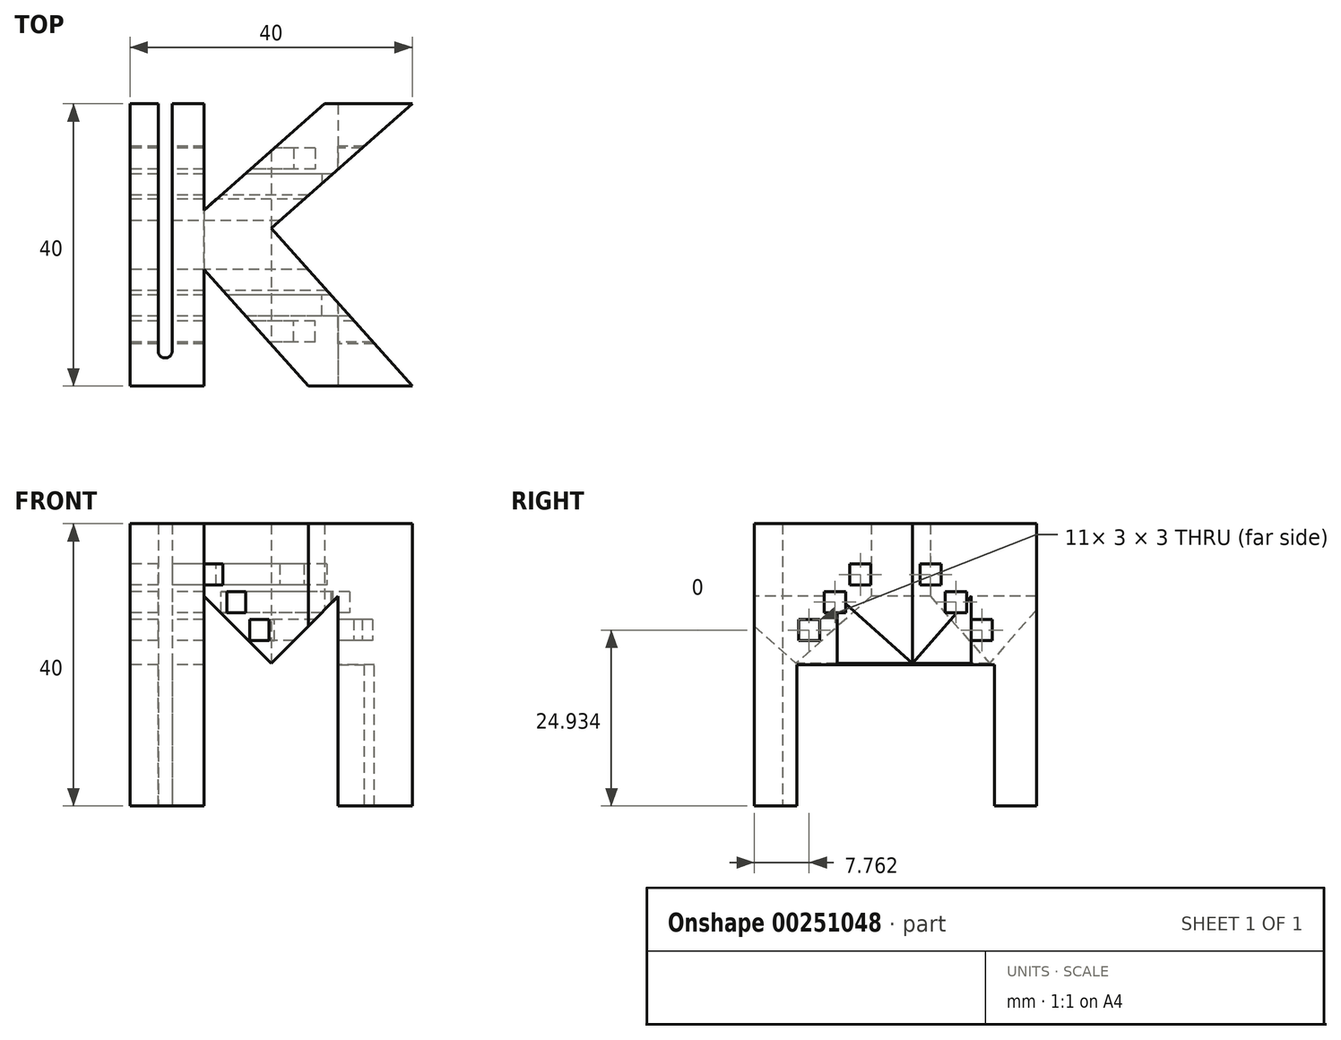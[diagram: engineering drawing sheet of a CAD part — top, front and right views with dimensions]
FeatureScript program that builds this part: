
annotation { "Feature Type Name" : "Feature", "Feature Type Description" : "" }
export const myFeature = defineFeature(function(context is Context, id is Id, definition is map)
    precondition{}
    {
        {
            var Q0;
            Q0=qCreatedBy(makeId("Top.planeOp"),FACE);
            var sketch = newSketch(context, id + "F0", { "sketchPlane" : qUnion([Q0])});
            skLineSegment(sketch, "E0.bottom", {"start": v(20, 20) * mm, "end": v(-20, 20) * mm});
            skLineSegment(sketch, "E0.top", {"start": v(20, -20) * mm, "end": v(-20, -20) * mm});
            skLineSegment(sketch, "E0.left", {"start": v(20, 20) * mm, "end": v(20, -20) * mm});
            skLineSegment(sketch, "E0.right", {"start": v(-20, 20) * mm, "end": v(-20, -20) * mm});
            skPoint(sketch, "E0.middle", {"position": v(0, 0) * mm});
            skLineSegment(sketch, "E1", {"start": v(-16, -15) * mm, "end": v(-16, 20) * mm});
            skLineSegment(sketch, "E2", {"start": v(-14, 20) * mm, "end": v(-14, -15) * mm});
            skLineSegment(sketch, "E3", {"start": v(-9.5, 20) * mm, "end": v(-9.5, -20) * mm});
            skLineSegment(sketch, "E4", {"start": v(-9.5, 4.95) * mm, "end": v(7.58, 20) * mm});
            skLineSegment(sketch, "E5", {"start": v(20, 20) * mm, "end": v(0, 2.39) * mm});
            skLineSegment(sketch, "E6", {"start": v(0, 2.39) * mm, "end": v(20, -20) * mm});
            skLineSegment(sketch, "E7", {"start": v(-9.5, -3.45) * mm, "end": v(5.28, -20) * mm});
            skArc(sketch, "E8", {"start": v(-16, -15) * mm, "mid": v(-15, -16) * mm, "end": v(-14, -15) * mm});
            skSolve(sketch);
        }
        {
            var Q0;
            {var subQ0=sQuery(id+"F0.wireOp",EDGE,"E4");Q0=makeQuery(id+"F0.imprint","IMPRINT",FACE,{"disambiguationData":[TD([[makeQuery(id+"F0.imprint","IMPRINT",EDGE,{"derivedFrom":subQ0}),-1.0]])]});}
            var Q1;
            {var subQ4=sQuery(id+"F0.wireOp",EDGE,"E2");Q1=makeQuery(id+"F0.imprint","IMPRINT",FACE,{"disambiguationData":[TD([[makeQuery(id+"F0.imprint","IMPRINT",EDGE,{"derivedFrom":subQ4}),1.0]])]});}
            var Q2;
            {var subQ0=sQuery(id+"F0.wireOp",EDGE,"E0.right");Q2=makeQuery(id+"F0.imprint","IMPRINT",FACE,{"disambiguationData":[TD([[makeQuery(id+"F0.imprint","IMPRINT",EDGE,{"derivedFrom":subQ0}),1.0]])]});}
            extrude(context, id + "F1", {"entities" : qUnion([Q0, Q1, Q2]), "depth" : 40 * mm});
        }
        {
            var Q0;
            Q0=makeQuery(id+"F1.opExtrude","SWEPT_FACE",FACE,{"disambiguationData":[OSD([sQuery(id+"F0.wireOp",EDGE,"E0.right")])]});
            var sketch = newSketch(context, id + "F2", { "sketchPlane" : qUnion([Q0])});
            skLineSegment(sketch, "E9", {"start": v(-14, 0) * mm, "end": v(-14, 20) * mm});
            skLineSegment(sketch, "E10", {"start": v(-14, 20) * mm, "end": v(14, 20) * mm});
            skLineSegment(sketch, "E11", {"start": v(14, 20) * mm, "end": v(14, 0) * mm});
            skLineSegment(sketch, "E12.bottom", {"start": v(-10.74, 23.43) * mm, "end": v(-13.74, 23.43) * mm});
            skLineSegment(sketch, "E12.top", {"start": v(-10.74, 26.43) * mm, "end": v(-13.74, 26.43) * mm});
            skLineSegment(sketch, "E12.left", {"start": v(-10.74, 23.43) * mm, "end": v(-10.74, 26.43) * mm});
            skLineSegment(sketch, "E12.right", {"start": v(-13.74, 23.43) * mm, "end": v(-13.74, 26.43) * mm});
            skPoint(sketch, "E12.middle", {"position": v(-12.24, 24.93) * mm});
            skLineSegment(sketch, "E13.bottom", {"start": v(-7.08, 27.4) * mm, "end": v(-10.08, 27.4) * mm});
            skLineSegment(sketch, "E13.top", {"start": v(-7.08, 30.4) * mm, "end": v(-10.08, 30.4) * mm});
            skLineSegment(sketch, "E13.left", {"start": v(-7.08, 27.4) * mm, "end": v(-7.08, 30.4) * mm});
            skLineSegment(sketch, "E13.right", {"start": v(-10.08, 27.4) * mm, "end": v(-10.08, 30.4) * mm});
            skPoint(sketch, "E13.middle", {"position": v(-8.58, 28.9) * mm});
            skLineSegment(sketch, "E14.bottom", {"start": v(-3.47, 31.3) * mm, "end": v(-6.47, 31.3) * mm});
            skLineSegment(sketch, "E14.top", {"start": v(-3.47, 34.3) * mm, "end": v(-6.47, 34.3) * mm});
            skLineSegment(sketch, "E14.left", {"start": v(-3.47, 31.3) * mm, "end": v(-3.47, 34.3) * mm});
            skLineSegment(sketch, "E14.right", {"start": v(-6.47, 31.3) * mm, "end": v(-6.47, 34.3) * mm});
            skPoint(sketch, "E14.middle", {"position": v(-4.97, 32.8) * mm});
            skLineSegment(sketch, "E15.MirrorCS", {"start": v(3.47, 31.3) * mm, "end": v(3.47, 34.3) * mm});
            skLineSegment(sketch, "E16.MirrorCS", {"start": v(3.47, 34.3) * mm, "end": v(6.47, 34.3) * mm});
            skLineSegment(sketch, "E17.MirrorCS", {"start": v(6.47, 31.3) * mm, "end": v(6.47, 34.3) * mm});
            skLineSegment(sketch, "E18.MirrorCS", {"start": v(3.47, 31.3) * mm, "end": v(6.47, 31.3) * mm});
            skLineSegment(sketch, "E19.MirrorCS", {"start": v(7.08, 30.4) * mm, "end": v(10.08, 30.4) * mm});
            skLineSegment(sketch, "E20.MirrorCS", {"start": v(10.08, 27.4) * mm, "end": v(10.08, 30.4) * mm});
            skLineSegment(sketch, "E21.MirrorCS", {"start": v(7.08, 27.4) * mm, "end": v(10.08, 27.4) * mm});
            skLineSegment(sketch, "E22.MirrorCS", {"start": v(7.08, 27.4) * mm, "end": v(7.08, 30.4) * mm});
            skLineSegment(sketch, "E23.MirrorCS", {"start": v(13.74, 23.43) * mm, "end": v(13.74, 26.43) * mm});
            skPoint(sketch, "E24.MirrorP", {"position": v(12.24, 24.93) * mm});
            skLineSegment(sketch, "E25.MirrorCS", {"start": v(10.74, 23.43) * mm, "end": v(13.74, 23.43) * mm});
            skLineSegment(sketch, "E26.MirrorCS", {"start": v(10.74, 23.43) * mm, "end": v(10.74, 26.43) * mm});
            skLineSegment(sketch, "E27.MirrorCS", {"start": v(10.74, 26.43) * mm, "end": v(13.74, 26.43) * mm});
            skPoint(sketch, "E28.MirrorP", {"position": v(8.58, 28.9) * mm});
            skPoint(sketch, "E29.MirrorP", {"position": v(4.97, 32.8) * mm});
            skSolve(sketch);
        }
        {
            var Q0;
            {var subQ0=sQuery(id+"F2.wireOp",EDGE,"E9");Q0=makeQuery(id+"F2.imprint","IMPRINT",FACE,{"disambiguationData":[TD([[makeQuery(id+"F2.imprint","IMPRINT",EDGE,{"derivedFrom":subQ0}),-1.0]])]});}
            extrude(context, id + "F3", {"entities" : qUnion([Q0]), "operationType" : NewBodyOperationType.REMOVE, "oppositeDirection" : true, "depth" : 40 * mm});
        }
        {
            var Q0;
            {var subQ0=sQuery(id+"F0.wireOp",EDGE,"E0.top");Q0=makeQuery(id+"F1.opExtrude","SWEPT_FACE",FACE,{"disambiguationData":[OSD([subQ0]),TDD([makeQuery(id+"F0.imprint","IMPRINT",EDGE,{"disambiguationData":[TD([[makeQuery(id+"F0.imprint","INTERSECT",VERTEX,{"derivedFrom":[subQ0,sQuery(id+"F0.wireOp",EDGE,"E0.right")]}),1.0]])],"derivedFrom":subQ0})])]});}
            var sketch = newSketch(context, id + "F4", { "sketchPlane" : qUnion([Q0])});
            skLineSegment(sketch, "E30", {"start": v(0, 20.21) * mm, "end": v(-9.5, 29.72) * mm});
            skLineSegment(sketch, "E31", {"start": v(0, 20.21) * mm, "end": v(9.5, 29.72) * mm});
            skLineSegment(sketch, "E32", {"start": v(9.5, 29.72) * mm, "end": v(9.5, 0) * mm});
            skLineSegment(sketch, "E33", {"start": v(-9.5, 29.72) * mm, "end": v(-9.5, 0) * mm});
            skLineSegment(sketch, "E34", {"start": v(-9.5, 0) * mm, "end": v(-20, 0) * mm});
            skLineSegment(sketch, "E35", {"start": v(-20, 0) * mm, "end": v(-20, 40) * mm});
            skLineSegment(sketch, "E36", {"start": v(-20, 40) * mm, "end": v(20, 40) * mm});
            skLineSegment(sketch, "E37", {"start": v(20, 40) * mm, "end": v(20, 0) * mm});
            skLineSegment(sketch, "E38", {"start": v(20, 0) * mm, "end": v(9.5, 0) * mm});
            skLineSegment(sketch, "E39", {"start": v(-9.5, 0) * mm, "end": v(9.5, 0) * mm});
            skSolve(sketch);
        }
        {
            var Q0;
            Q0=makeQuery(id+"F4.imprint","IMPRINT",FACE,{"disambiguationData":[TD([[makeQuery(id+"F4.imprint","IMPRINT",EDGE,{"derivedFrom":sQuery(id+"F4.wireOp",EDGE,"E30")}),1.0]])]});
            extrude(context, id + "F5", {"entities" : qUnion([Q0]), "operationType" : NewBodyOperationType.REMOVE, "oppositeDirection" : true, "depth" : 40 * mm});
        }
        {
            var Q0;
            Q0=makeQuery(id+"F2.imprint","IMPRINT",FACE,{"disambiguationData":[TD([[makeQuery(id+"F2.imprint","IMPRINT",EDGE,{"derivedFrom":sQuery(id+"F2.wireOp",EDGE,"E14.bottom")}),-1.0]])]});
            var Q1;
            Q1=makeQuery(id+"F2.imprint","IMPRINT",FACE,{"disambiguationData":[TD([[makeQuery(id+"F2.imprint","IMPRINT",EDGE,{"derivedFrom":sQuery(id+"F2.wireOp",EDGE,"E15.MirrorCS")}),-1.0]])]});
            var Q2;
            Q2=makeQuery(id+"F2.imprint","IMPRINT",FACE,{"disambiguationData":[TD([[makeQuery(id+"F2.imprint","IMPRINT",EDGE,{"derivedFrom":sQuery(id+"F2.wireOp",EDGE,"E13.bottom")}),-1.0]])]});
            var Q3;
            Q3=makeQuery(id+"F2.imprint","IMPRINT",FACE,{"disambiguationData":[TD([[makeQuery(id+"F2.imprint","IMPRINT",EDGE,{"derivedFrom":sQuery(id+"F2.wireOp",EDGE,"E12.bottom")}),-1.0]])]});
            var Q4;
            Q4=makeQuery(id+"F2.imprint","IMPRINT",FACE,{"disambiguationData":[TD([[makeQuery(id+"F2.imprint","IMPRINT",EDGE,{"derivedFrom":sQuery(id+"F2.wireOp",EDGE,"E19.MirrorCS")}),-1.0]])]});
            var Q5;
            Q5=makeQuery(id+"F2.imprint","IMPRINT",FACE,{"disambiguationData":[TD([[makeQuery(id+"F2.imprint","IMPRINT",EDGE,{"derivedFrom":sQuery(id+"F2.wireOp",EDGE,"E23.MirrorCS")}),1.0]])]});
            extrude(context, id + "F6", {"entities" : qUnion([Q0, Q1, Q2, Q3, Q4, Q5]), "operationType" : NewBodyOperationType.REMOVE, "oppositeDirection" : true, "depth" : 40 * mm});
        }
    });
